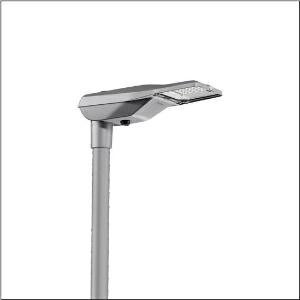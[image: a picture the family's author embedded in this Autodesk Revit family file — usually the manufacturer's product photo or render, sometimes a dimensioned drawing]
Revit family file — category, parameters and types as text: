
# Revit family: streetlight_sl_21_iq_micro___st1_0a_5xe1d31u08db_5c5a
name_source: partatom
category: Lighting Fixtures
units: mm (PartAtom-declared; Revit-internal decimal feet)

## family parameters
Cut with Voids When Loaded = No
Host = Face
Light Source = No
Part Type = Normal
Room Calculation Point = No
Round Connector Dimension = Use Diameter
Shared = No

## types (1)
- --- (1 x LED, 5110 lm, 39.1 W, 3000K)
    Apparent Load = 39 VA
    CIE Flux Codes = 37 72 97 100 100
    Color Rendering = 70
    Color Temperature = 3000K
    Default Elevation = 1800 mm
    Description = Streetlight SL 21 iQ micro, mast luminaire, primary light control with lens, of PMMA, primary optical cover: cover, of toughened safety glass, transparent, light distribution: ST1.0a, light emission: direct distribution, primary light characteristic: asymmetric, installation type: post-top, side-entry, LED, High Power LED, rated luminous flux: 5.110lm, luminous efficacy: 131lm/W, light colour: 730, colour temperature: 3000K, control: presetting dimming logarithmic, Street-Remote, Auto-Match, Temp-Guard, Lumen-Switch, Night-Set, Smart-Wire, Light-Fading, Desk-Remote (wireless, voltage-free reading and setting of iQ features in the workshop via application-optimized NFC function/RFID function), optimised constant luminous flux control (CLO 2.0), mains connection: 220..240V, AC, 50/60Hz, start of lifetime: 39W, end of service life: 41W, reduction: 17W, luminaire housing, of diecast aluminium, powder-coated, Siteco® metallic grey (DB 702S), corrosivity category C5 mid according to DIN EN ISO 12944, please order mast flange separately, inclination adjustable: 0°, 5°, 10°, 15°, sealing non-destructively replaceable, multi-level sealing system, length: 528mm, width: 235mm, height: 110mm, mast flange for spigot size: 42mm (side-entry): 5XC10008XM4, 60/48mm (side-entry/post-top): 5XC10108XM2, 76/60mm (side-entry/post-top): 5XC10108XM1, Smart Interface below, protection rating (complete): IP66, insulation class (complete): insulation class II (safety insulation), certification: CE, ENEC, ENEC+, VDE, impact resistance: IK09, permissible operating ambient temperature for outdoor applications: -40..+50°C, standard-compliant lighting for roads and squares, packaging unit: 1 piece

Light Distribution: ST1.0a
    Height = 110 mm
    Lamp = 1 x LED
    Lamp Light Flux = 5110 lm
    Lamp Power = 39.1 W
    Lamp count = 1
    Length = 528 mm
    Luminous efficacy = 131 lm/W
    Manufacturer = Siteco
    ModVariant = No
    Model = 5XE1D31U08DB
    Number of Poles = 1
    OnlyDefault = Yes
    Power Factor = 1
    Product Name = Streetlight SL 21 iQ micro | ST1.0a
    Product group = mast luminaire | pylon top
    ProductGroupID = 6100
    Protection Class = Protection class II
    Protection Degree = IP 66
    RLX_Detail_Level = 1
    RLX_Emergency_Light_Flux = 0 lm
    RLX_Emergency_Type = 0
    RLX_Emergency_Type_DB = No
    RlxData = <blob elided: 98813 chars, md5=7f5d56f7>
    Socket = socket
    Standby Power = 0 W
    System Light Flux = 5110 lm
    System Power = 39 W
    Type Comments = factory setting: luminous flux: 100 % | dim-lin: 254 | 765 mA
    Type Image = l_1277290.jpg
    URL = http://relux.com
    VarID = @adj_045761
    Voltage = 0 V
    Weight = 0.00 kg
    Width = 235 mm

## geometry (parser evidence)
native form markers: Blend x4, Sweep x10
no freeform markers — native parametric forms only
